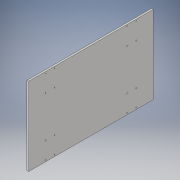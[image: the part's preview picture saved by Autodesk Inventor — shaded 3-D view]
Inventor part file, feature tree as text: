
AUTODESK INVENTOR PART (.ipt)
format: ipt  version: 2017 (Build 210142000, 142)  size: 139,264 bytes
history: native  units: in
note: dims shown in document units (in); Inventor stores cm internally (conversion verified against a paired STEP export)
features: extrude x1, sketch x1
ambient origin geometry x8: Origin, YZ Plane, XZ Plane, XY Plane, X Axis, Y Axis, Z Axis, Center Point
bodies: Solid1 (feature_tree)
feature tree (2):
  extrude  "Extrusion1"  Depth=17.5in
  sketch  "Sketch1"  dims[d0=11.0in d1=17.5in d2=0.13in d3=0.13in d4=1.26in d5=0.236in d6=0.236in d7=2.37in d8=0.13in d9=0.13in d10=2.364in d11=2.364in d12=2.37in d13=0.13in d14=0.13in d15=0.13in d16=0.13in d17=2.37in d18=2.37in d19=0.236in d20=0.236in d22=2.364in d23=2.364in d24=1.26in d25=0.13in d26=0.13in d27=0.236in d28=0.236in d29=0.13in d30=0.13in d32=1.26in d33=1.26in d34=2.37in d35=2.37in d36=0.13in d37=0.13in d38=0.13in d39=0.13in d40=0.25in d41=0.0in]
